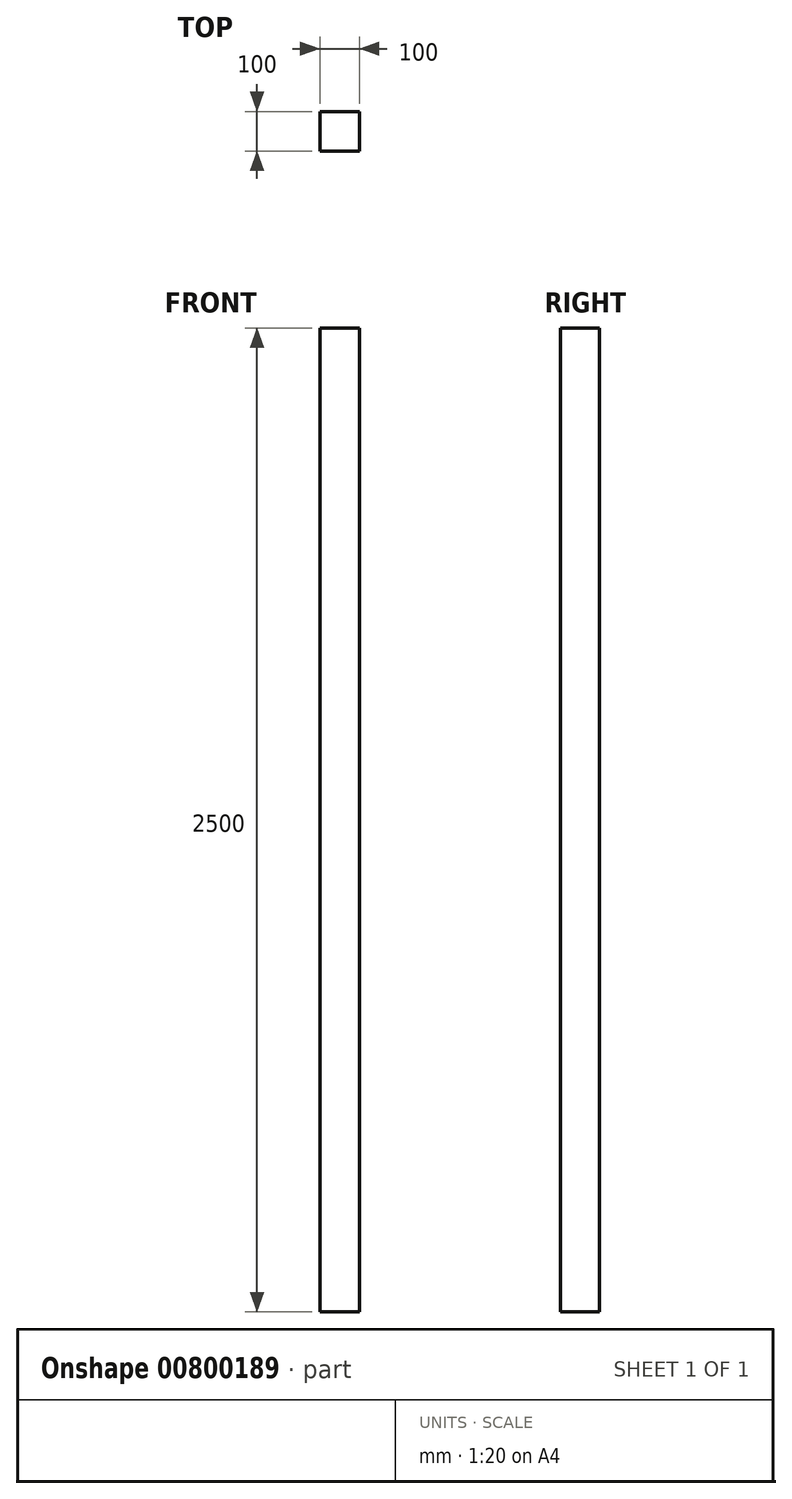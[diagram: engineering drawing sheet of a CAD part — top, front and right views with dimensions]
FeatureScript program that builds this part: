
annotation { "Feature Type Name" : "Feature", "Feature Type Description" : "" }
export const myFeature = defineFeature(function(context is Context, id is Id, definition is map)
    precondition{}
    {
        {
            var Q0;
            Q0=qCreatedBy(makeId("Front.planeOp"),FACE);
            var sketch = newSketch(context, id + "F0", { "sketchPlane" : qUnion([Q0])});
            skLineSegment(sketch, "E0.bottom", {"start": v(-76.53, 2125.03) * mm, "end": v(23.47, 2125.03) * mm});
            skLineSegment(sketch, "E0.top", {"start": v(-76.53, -374.97) * mm, "end": v(23.47, -374.97) * mm});
            skLineSegment(sketch, "E0.left", {"start": v(-76.53, 2125.03) * mm, "end": v(-76.53, -374.97) * mm});
            skLineSegment(sketch, "E0.right", {"start": v(23.47, 2125.03) * mm, "end": v(23.47, -374.97) * mm});
            skSolve(sketch);
        }
        {
            var Q0;
            Q0=makeQuery(id+"F0.imprint","IMPRINT",FACE,{"disambiguationData":[TD([[makeQuery(id+"F0.imprint","IMPRINT",EDGE,{"derivedFrom":sQuery(id+"F0.wireOp",EDGE,"E0.bottom")}),-1.0]])]});
            extrude(context, id + "F1", {"entities" : qUnion([Q0]), "endBound" : BoundingType.SYMMETRIC, "oppositeDirection" : true, "depth" : 100 * mm, "offsetDistance" : 25 * mm});
        }
    });
